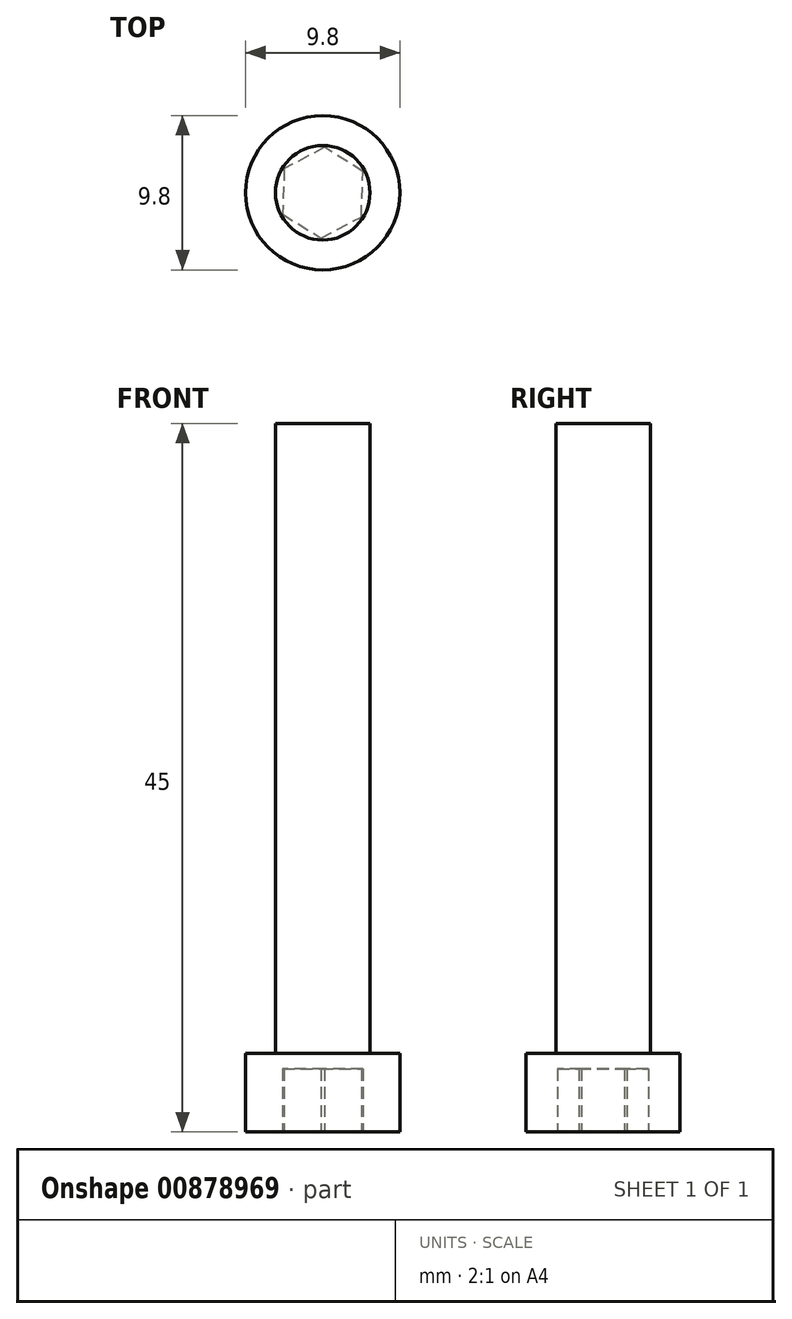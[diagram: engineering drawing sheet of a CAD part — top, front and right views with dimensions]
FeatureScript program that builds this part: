
annotation { "Feature Type Name" : "Feature", "Feature Type Description" : "" }
export const myFeature = defineFeature(function(context is Context, id is Id, definition is map)
    precondition{}
    {
        {
            var Q0;
            Q0=qCreatedBy(makeId("Top.planeOp"),FACE);
            var sketch = newSketch(context, id + "F0", { "sketchPlane" : qUnion([Q0])});
            skCircle(sketch, "E0", {"center": v(0, 0) * mm, "radius": 3 * mm});
            skSolve(sketch);
        }
        {
            var Q0;
            Q0 = qSketchRegion(id + "F0", true);
            extrude(context, id + "F1", {"entities" : qUnion([Q0]), "depth" : 40 * mm, "offsetDistance" : 25 * mm});
        }
        {
            var Q0;
            Q0=makeQuery(id+"F1.opExtrude","CAP_FACE",FACE,{"disambiguationData":[OSD([sQuery(id+"F0.wireOp",EDGE,"E0")])],"isStart":true});
            var sketch = newSketch(context, id + "F2", { "sketchPlane" : qUnion([Q0])});
            skCircle(sketch, "E1", {"center": v(0, 0) * mm, "radius": 4.9 * mm});
            skSolve(sketch);
        }
        {
            var Q0;
            Q0 = qSketchRegion(id + "F2", true);
            extrude(context, id + "F3", {"entities" : qUnion([Q0]), "operationType" : NewBodyOperationType.ADD, "depth" : 5 * mm, "offsetDistance" : 25 * mm});
        }
        {
            var Q0;
            Q0=makeQuery(id+"F3.opExtrude","CAP_FACE",FACE,{"disambiguationData":[OSD([sQuery(id+"F2.wireOp",EDGE,"E1")])],"isStart":false});
            var sketch = newSketch(context, id + "F4", { "sketchPlane" : qUnion([Q0])});
            skCircle(sketch, "E2.cCircle", {"center": v(0, 0) * mm, "radius": 2.5 * mm, "construction": true});
            skLineSegment(sketch, "E2.0", {"start": v(-0.1, 2.89) * mm, "end": v(2.45, 1.53) * mm});
            skLineSegment(sketch, "E2.1", {"start": v(2.45, 1.53) * mm, "end": v(2.55, -1.36) * mm});
            skLineSegment(sketch, "E2.2", {"start": v(2.55, -1.36) * mm, "end": v(0.1, -2.89) * mm});
            skLineSegment(sketch, "E2.3", {"start": v(0.1, -2.89) * mm, "end": v(-2.45, -1.53) * mm});
            skLineSegment(sketch, "E2.4", {"start": v(-2.45, -1.53) * mm, "end": v(-2.55, 1.36) * mm});
            skLineSegment(sketch, "E2.5", {"start": v(-2.55, 1.36) * mm, "end": v(-0.1, 2.89) * mm});
            skPoint(sketch, "E2.0.midPoint", {"position": v(1.17, 2.2) * mm});
            skSolve(sketch);
        }
        {
            var Q0;
            Q0 = qSketchRegion(id + "F4", true);
            extrude(context, id + "F5", {"entities" : qUnion([Q0]), "operationType" : NewBodyOperationType.REMOVE, "oppositeDirection" : true, "depth" : 4 * mm, "offsetDistance" : 25 * mm});
        }
    });
